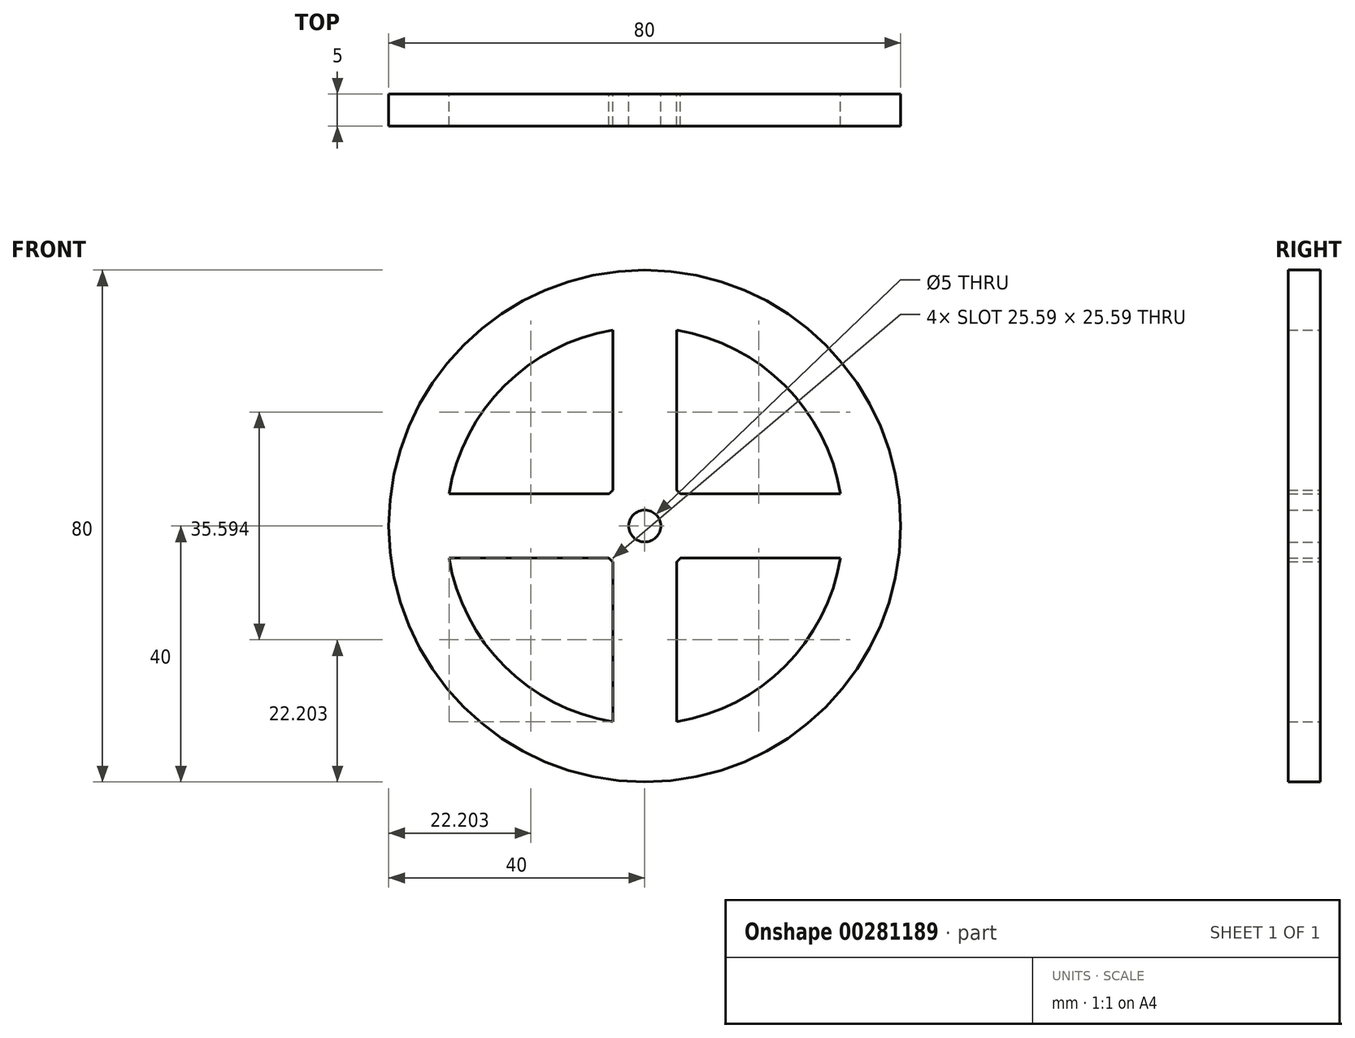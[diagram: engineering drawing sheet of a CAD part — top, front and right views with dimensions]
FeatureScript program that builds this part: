
annotation { "Feature Type Name" : "Feature", "Feature Type Description" : "" }
export const myFeature = defineFeature(function(context is Context, id is Id, definition is map)
    precondition{}
    {
        {
            var Q0;
            Q0=qCreatedBy(makeId("Front.planeOp"),FACE);
            var sketch = newSketch(context, id + "F0", { "sketchPlane" : qUnion([Q0])});
            skCircle(sketch, "E0", {"center": v(0, 0) * mm, "radius": 40 * mm});
            skArc(sketch, "E1", {"start": v(-5, 30.6) * mm, "mid": v(-21.92, 21.92) * mm, "end": v(-30.6, 5) * mm});
            skArc(sketch, "E2", {"start": v(-5.6, -5) * mm, "mid": v(-5.3, -5.3) * mm, "end": v(-5, -5.6) * mm});
            skCircle(sketch, "E3", {"center": v(0, 0) * mm, "radius": 2.5 * mm});
            skLineSegment(sketch, "E4", {"start": v(0, 0) * mm, "end": v(0, 2.5) * mm});
            skLineSegment(sketch, "E5", {"start": v(0, 0) * mm, "end": v(-31, 0) * mm, "construction": true});
            skLineSegment(sketch, "E6", {"start": v(0, 0) * mm, "end": v(0, -2.5) * mm});
            skLineSegment(sketch, "E7", {"start": v(0, 0) * mm, "end": v(31, 0) * mm, "construction": true});
            skLineSegment(sketch, "E8.0", {"start": v(5, 5.6) * mm, "end": v(5, 30.6) * mm});
            skLineSegment(sketch, "E9.0", {"start": v(-5, 5.6) * mm, "end": v(-5, 30.6) * mm});
            skLineSegment(sketch, "E10.0", {"start": v(-5.6, 5) * mm, "end": v(-30.6, 5) * mm});
            skLineSegment(sketch, "E11.0", {"start": v(-5.6, -5) * mm, "end": v(-30.6, -5) * mm});
            skLineSegment(sketch, "E12.0", {"start": v(-5, -5.6) * mm, "end": v(-5, -30.6) * mm});
            skLineSegment(sketch, "E13.0", {"start": v(5, -5.6) * mm, "end": v(5, -30.6) * mm});
            skLineSegment(sketch, "E14.0", {"start": v(5.6, -5) * mm, "end": v(30.6, -5) * mm});
            skLineSegment(sketch, "E15.0", {"start": v(5.6, 5) * mm, "end": v(30.6, 5) * mm});
            skArc(sketch, "E16.trimOffspring", {"start": v(30.6, 5) * mm, "mid": v(21.92, 21.92) * mm, "end": v(5, 30.6) * mm});
            skArc(sketch, "E17.trimOffspring", {"start": v(5, -30.6) * mm, "mid": v(21.92, -21.92) * mm, "end": v(30.6, -5) * mm});
            skArc(sketch, "E18.trimOffspring", {"start": v(-30.6, -5) * mm, "mid": v(-21.92, -21.92) * mm, "end": v(-5, -30.6) * mm});
            skArc(sketch, "E19.trimOffspring", {"start": v(-5, 5.6) * mm, "mid": v(-5.3, 5.3) * mm, "end": v(-5.6, 5) * mm});
            skArc(sketch, "E20.trimOffspring", {"start": v(5.6, 5) * mm, "mid": v(5.3, 5.3) * mm, "end": v(5, 5.6) * mm});
            skArc(sketch, "E21.trimOffspring", {"start": v(5, -5.6) * mm, "mid": v(5.3, -5.3) * mm, "end": v(5.6, -5) * mm});
            skLineSegment(sketch, "E22.trimOffspring", {"start": v(0, 5) * mm, "end": v(0, 31) * mm, "construction": true});
            skLineSegment(sketch, "E23.trimOffspring", {"start": v(0, -5) * mm, "end": v(0, -31) * mm, "construction": true});
            skSolve(sketch);
        }
        {
            var Q0;
            Q0 = qSketchRegion(id + "F0", true);
            extrude(context, id + "F1", {"entities" : qUnion([Q0]), "endBound" : BoundingType.SYMMETRIC, "depth" : 5 * mm});
        }
    });
